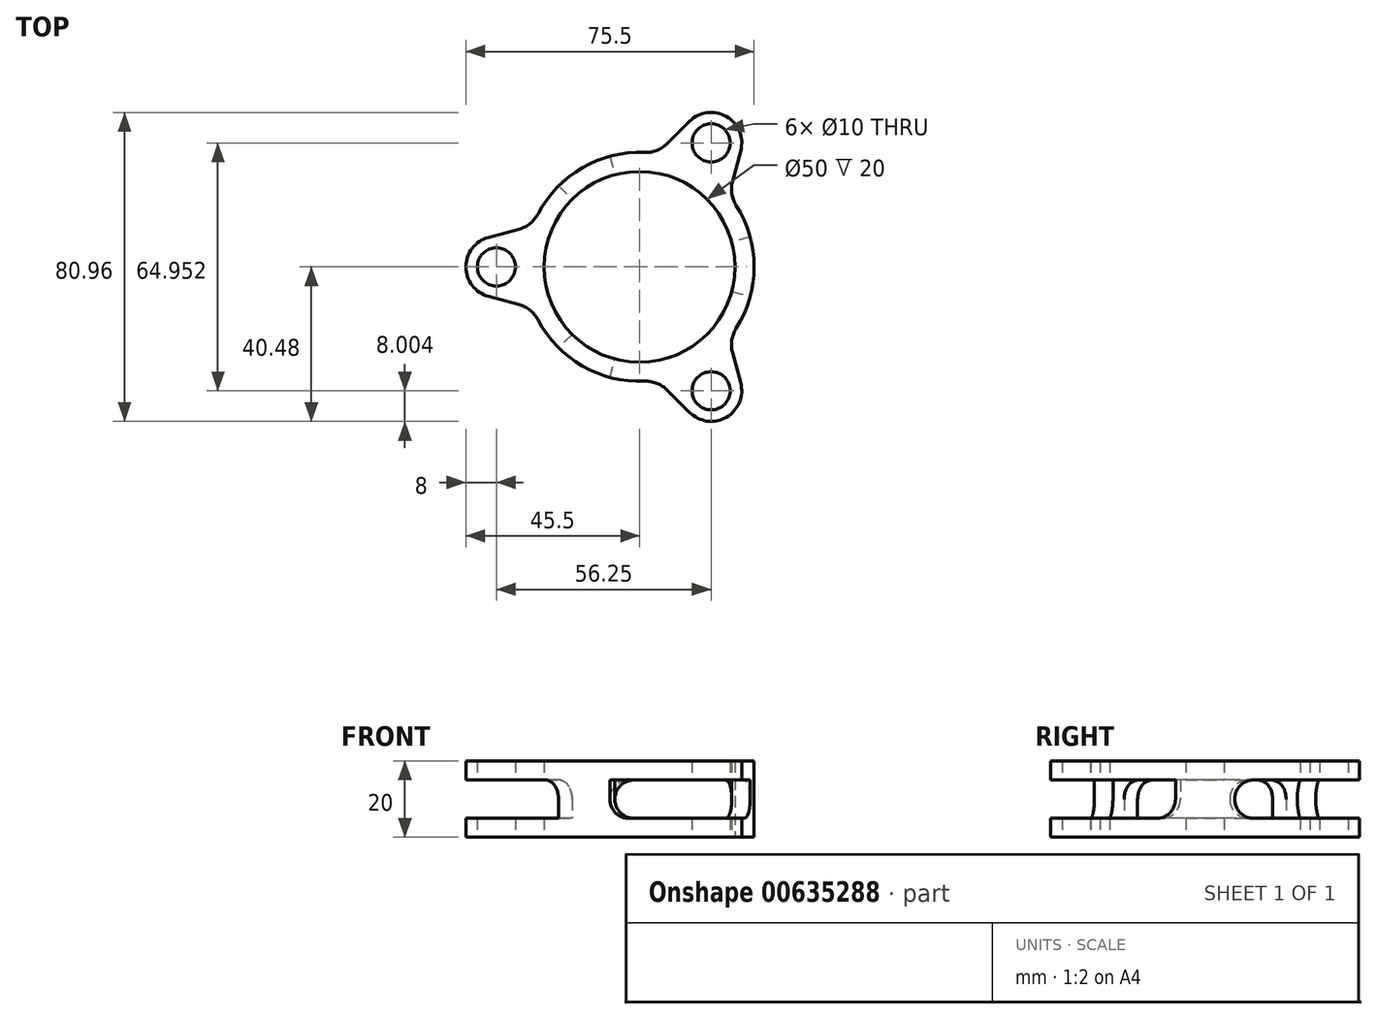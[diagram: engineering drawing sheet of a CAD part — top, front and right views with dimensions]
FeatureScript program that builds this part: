
annotation { "Feature Type Name" : "Feature", "Feature Type Description" : "" }
export const myFeature = defineFeature(function(context is Context, id is Id, definition is map)
    precondition{}
    {
        {
            var Q0;
            Q0=qCreatedBy(makeId("Top.planeOp"),FACE);
            var sketch = newSketch(context, id + "F0", { "sketchPlane" : qUnion([Q0])});
            skCircle(sketch, "E0", {"center": v(0, 0) * mm, "radius": 25 * mm});
            skCircle(sketch, "E1", {"center": v(0, 0) * mm, "radius": 30 * mm});
            skLineSegment(sketch, "E2", {"start": v(0, 0) * mm, "end": v(-50.3, 0) * mm, "construction": true});
            skLineSegment(sketch, "E3", {"start": v(0, 0) * mm, "end": v(23.8, 41.22) * mm, "construction": true});
            skLineSegment(sketch, "E4", {"start": v(0, 0) * mm, "end": v(24.89, -43.1) * mm, "construction": true});
            skCircle(sketch, "E5", {"center": v(0, 0) * mm, "radius": 37.5 * mm, "construction": true});
            skCircle(sketch, "E6", {"center": v(-37.5, 0) * mm, "radius": 5 * mm});
            skArc(sketch, "E7", {"start": v(-39.57, 7.73) * mm, "mid": v(-45.5, 0) * mm, "end": v(-39.57, -7.73) * mm});
            skLineSegment(sketch, "E8", {"start": v(-39.57, 7.73) * mm, "end": v(-31.61, 9.86) * mm});
            skLineSegment(sketch, "E9", {"start": v(-39.57, -7.73) * mm, "end": v(-31.61, -9.86) * mm});
            skArc(sketch, "E10", {"start": v(-26.6, -13.88) * mm, "mid": v(-28.68, -11.34) * mm, "end": v(-31.61, -9.86) * mm});
            skArc(sketch, "E11.MirrorCS", {"start": v(-26.6, 13.88) * mm, "mid": v(-28.68, 11.34) * mm, "end": v(-31.61, 9.86) * mm});
            skCircle(sketch, "E12.1.0", {"center": v(18.75, -32.48) * mm, "radius": 5 * mm});
            skArc(sketch, "E12.1.1", {"start": v(13.1, -38.13) * mm, "mid": v(22.75, -39.4) * mm, "end": v(26.48, -30.4) * mm});
            skLineSegment(sketch, "E12.1.2", {"start": v(26.48, -30.4) * mm, "end": v(24.35, -22.45) * mm});
            skLineSegment(sketch, "E12.1.3", {"start": v(13.1, -38.13) * mm, "end": v(7.27, -32.3) * mm});
            skArc(sketch, "E12.1.4", {"start": v(25.32, -16.09) * mm, "mid": v(24.17, -19.17) * mm, "end": v(24.35, -22.45) * mm});
            skArc(sketch, "E12.1.5", {"start": v(1.27, -29.97) * mm, "mid": v(4.52, -30.51) * mm, "end": v(7.27, -32.3) * mm});
            skCircle(sketch, "E12.2.0", {"center": v(18.75, 32.48) * mm, "radius": 5 * mm});
            skArc(sketch, "E12.2.1", {"start": v(26.48, 30.4) * mm, "mid": v(22.75, 39.4) * mm, "end": v(13.1, 38.13) * mm});
            skLineSegment(sketch, "E12.2.2", {"start": v(13.1, 38.13) * mm, "end": v(7.27, 32.3) * mm});
            skLineSegment(sketch, "E12.2.3", {"start": v(26.48, 30.4) * mm, "end": v(24.35, 22.45) * mm});
            skArc(sketch, "E12.2.4", {"start": v(1.27, 29.97) * mm, "mid": v(4.52, 30.51) * mm, "end": v(7.27, 32.3) * mm});
            skArc(sketch, "E12.2.5", {"start": v(25.32, 16.09) * mm, "mid": v(24.17, 19.17) * mm, "end": v(24.35, 22.45) * mm});
            skLineSegment(sketch, "E13", {"start": v(0, 0) * mm, "end": v(-33.56, 33.56) * mm, "construction": true});
            skLineSegment(sketch, "E14", {"start": v(0, 0) * mm, "end": v(-44.74, -44.74) * mm, "construction": true});
            skLineSegment(sketch, "E15", {"start": v(-21.21, 21.21) * mm, "end": v(-17.68, 17.68) * mm});
            skLineSegment(sketch, "E16", {"start": v(-17.68, -17.68) * mm, "end": v(-21.21, -21.21) * mm});
            skLineSegment(sketch, "E17.1.0", {"start": v(24.15, -6.47) * mm, "end": v(28.98, -7.76) * mm});
            skLineSegment(sketch, "E17.1.1", {"start": v(0, 0) * mm, "end": v(61.11, -16.38) * mm, "construction": true});
            skLineSegment(sketch, "E17.1.2", {"start": v(-7.76, -28.98) * mm, "end": v(-6.47, -24.15) * mm});
            skLineSegment(sketch, "E17.1.3", {"start": v(0, 0) * mm, "end": v(-12.28, -45.84) * mm, "construction": true});
            skLineSegment(sketch, "E17.2.0", {"start": v(-6.47, 24.15) * mm, "end": v(-7.76, 28.98) * mm});
            skLineSegment(sketch, "E17.2.1", {"start": v(0, 0) * mm, "end": v(-16.38, 61.11) * mm, "construction": true});
            skLineSegment(sketch, "E17.2.2", {"start": v(28.98, 7.76) * mm, "end": v(24.15, 6.47) * mm});
            skLineSegment(sketch, "E17.2.3", {"start": v(0, 0) * mm, "end": v(45.84, 12.28) * mm, "construction": true});
            skSolve(sketch);
        }
        {
            var Q0;
            Q0 = qSketchRegion(id + "F0", true);
            extrude(context, id + "F1", {"entities" : qUnion([Q0]), "depth" : 5 * mm, "offsetDistance" : 25 * mm});
        }
        {
            var Q0;
            {var subQ0=sQuery(id+"F0.wireOp",EDGE,"E17.1.0");Q0=makeQuery(id+"F0.imprint","IMPRINT",FACE,{"disambiguationData":[TD([[makeQuery(id+"F0.imprint","IMPRINT",EDGE,{"derivedFrom":subQ0}),1.0]])]});}
            var Q1;
            {var subQ0=sQuery(id+"F0.wireOp",EDGE,"E15");Q1=makeQuery(id+"F0.imprint","IMPRINT",FACE,{"disambiguationData":[TD([[makeQuery(id+"F0.imprint","IMPRINT",EDGE,{"derivedFrom":subQ0}),1.0]])]});}
            var Q2;
            {var subQ0=sQuery(id+"F0.wireOp",EDGE,"E16");Q2=makeQuery(id+"F0.imprint","IMPRINT",FACE,{"disambiguationData":[TD([[makeQuery(id+"F0.imprint","IMPRINT",EDGE,{"derivedFrom":subQ0}),1.0]])]});}
            extrude(context, id + "F2", {"entities" : qUnion([Q0, Q1, Q2]), "operationType" : NewBodyOperationType.ADD, "depth" : 15 * mm, "hasOffset" : true, "offsetDistance" : 5 * mm, "hasSecondDirection" : true, "secondDirectionOppositeDirection" : false, "secondDirectionDepth" : 5 * mm});
        }
        {
            var Q0;
            Q0 = qSketchRegion(id + "F0", true);
            extrude(context, id + "F3", {"entities" : qUnion([Q0]), "operationType" : NewBodyOperationType.ADD, "depth" : 20 * mm, "offsetDistance" : 25 * mm, "hasSecondDirection" : true, "secondDirectionOppositeDirection" : true, "secondDirectionDepth" : -15 * mm});
        }
        {
            var Q0;
            Q0=makeQuery(id+"F2.opExtrude","CAP_EDGE",EDGE,{"disambiguationData":[OSD([sQuery(id+"F0.wireOp",EDGE,"E17.1.2")])],"isStart":true});
            var Q1;
            Q1=makeQuery(id+"F2.opExtrude","CAP_EDGE",EDGE,{"disambiguationData":[OSD([sQuery(id+"F0.wireOp",EDGE,"E17.1.2")])],"isStart":false});
            var Q2;
            Q2=makeQuery(id+"F2.opExtrude","CAP_EDGE",EDGE,{"disambiguationData":[OSD([sQuery(id+"F0.wireOp",EDGE,"E17.1.0")])],"isStart":false});
            var Q3;
            Q3=makeQuery(id+"F2.opExtrude","CAP_EDGE",EDGE,{"disambiguationData":[OSD([sQuery(id+"F0.wireOp",EDGE,"E17.1.0")])],"isStart":true});
            var Q4;
            Q4=makeQuery(id+"F2.opExtrude","CAP_EDGE",EDGE,{"disambiguationData":[OSD([sQuery(id+"F0.wireOp",EDGE,"E17.2.2")])],"isStart":true});
            var Q5;
            Q5=makeQuery(id+"F2.opExtrude","CAP_EDGE",EDGE,{"disambiguationData":[OSD([sQuery(id+"F0.wireOp",EDGE,"E17.2.2")])],"isStart":false});
            var Q6;
            Q6=makeQuery(id+"F2.opExtrude","CAP_EDGE",EDGE,{"disambiguationData":[OSD([sQuery(id+"F0.wireOp",EDGE,"E16")])],"isStart":false});
            var Q7;
            Q7=makeQuery(id+"F2.opExtrude","CAP_EDGE",EDGE,{"disambiguationData":[OSD([sQuery(id+"F0.wireOp",EDGE,"E16")])],"isStart":true});
            var Q8;
            Q8=makeQuery(id+"F2.opExtrude","CAP_EDGE",EDGE,{"disambiguationData":[OSD([sQuery(id+"F0.wireOp",EDGE,"E15")])],"isStart":true});
            var Q9;
            Q9=makeQuery(id+"F2.opExtrude","CAP_EDGE",EDGE,{"disambiguationData":[OSD([sQuery(id+"F0.wireOp",EDGE,"E15")])],"isStart":false});
            var Q10;
            Q10=makeQuery(id+"F2.opExtrude","CAP_EDGE",EDGE,{"disambiguationData":[OSD([sQuery(id+"F0.wireOp",EDGE,"E17.2.0")])],"isStart":false});
            var Q11;
            Q11=makeQuery(id+"F2.opExtrude","CAP_EDGE",EDGE,{"disambiguationData":[OSD([sQuery(id+"F0.wireOp",EDGE,"E17.2.0")])],"isStart":true});
            fillet(context, id + "F4", {"entities" : qUnion([Q0, Q1, Q2, Q3, Q4, Q5, Q6, Q7, Q8, Q9, Q10, Q11]), "radius" : 5 * mm, "allowEdgeOverflow" : false});
        }
    });
